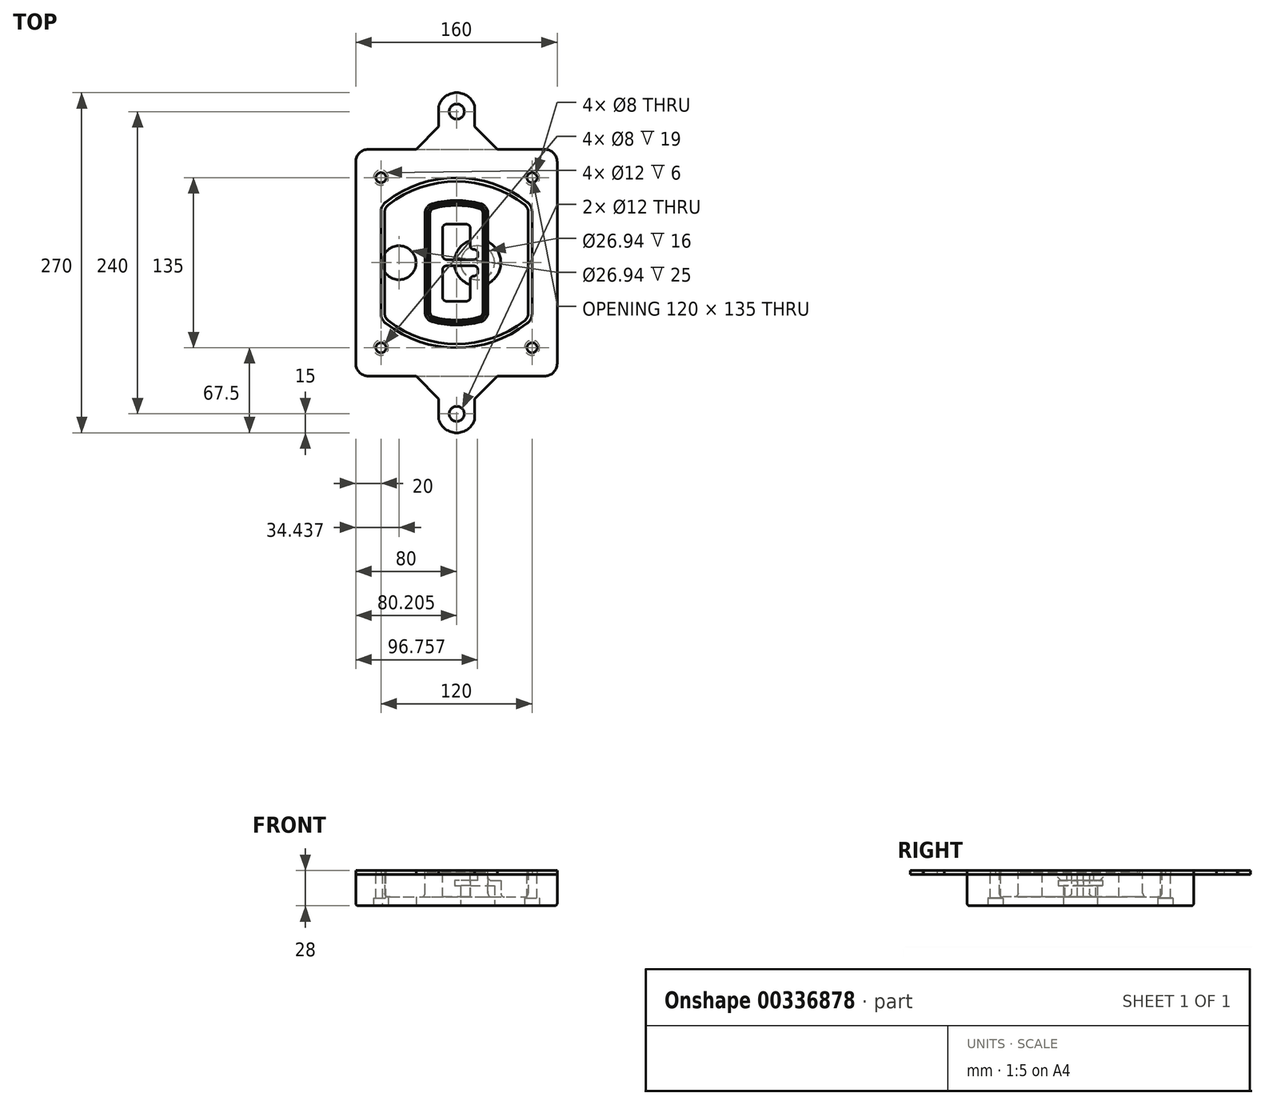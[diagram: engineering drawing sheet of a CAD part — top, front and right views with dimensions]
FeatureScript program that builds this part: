
annotation { "Feature Type Name" : "Feature", "Feature Type Description" : "" }
export const myFeature = defineFeature(function(context is Context, id is Id, definition is map)
    precondition{}
    {
        {
            var Q0;
            Q0=qCreatedBy(makeId("Top.planeOp"),FACE);
            var sketch = newSketch(context, id + "F0", { "sketchPlane" : qUnion([Q0])});
            skPoint(sketch, "E0.rect.middle", {"position": v(0, 0) * mm});
            skLineSegment(sketch, "E1.bottom", {"start": v(-70, -90) * mm, "end": v(70, -90) * mm});
            skLineSegment(sketch, "E1.top", {"start": v(-70, 90) * mm, "end": v(70, 90) * mm});
            skLineSegment(sketch, "E1.left", {"start": v(-80, -80) * mm, "end": v(-80, 80) * mm});
            skLineSegment(sketch, "E1.right", {"start": v(80, -80) * mm, "end": v(80, 80) * mm});
            skLineSegment(sketch, "E2", {"start": v(-80, 90) * mm, "end": v(80, -90) * mm, "construction": true});
            skLineSegment(sketch, "E3", {"start": v(80, 90) * mm, "end": v(-80, -90) * mm, "construction": true});
            skCircle(sketch, "E4", {"center": v(-60, 67.5) * mm, "radius": 4 * mm});
            skCircle(sketch, "E5", {"center": v(60, 67.5) * mm, "radius": 4 * mm});
            skCircle(sketch, "E6", {"center": v(60, -67.5) * mm, "radius": 4 * mm});
            skCircle(sketch, "E7", {"center": v(-60, -67.5) * mm, "radius": 4 * mm});
            skLineSegment(sketch, "E8", {"start": v(-60, 67.5) * mm, "end": v(60, 67.5) * mm, "construction": true});
            skLineSegment(sketch, "E9", {"start": v(60, 67.5) * mm, "end": v(60, -67.5) * mm, "construction": true});
            skLineSegment(sketch, "E10", {"start": v(60, -67.5) * mm, "end": v(-60, -67.5) * mm, "construction": true});
            skLineSegment(sketch, "E11", {"start": v(-60, -67.5) * mm, "end": v(-60, 67.5) * mm, "construction": true});
            skLineSegment(sketch, "E12", {"start": v(-60, 40.3) * mm, "end": v(-60, -40.3) * mm});
            skLineSegment(sketch, "E13", {"start": v(60, 40.3) * mm, "end": v(60, -40.3) * mm});
            skArc(sketch, "E14", {"start": v(56.15, 48.18) * mm, "mid": v(0, 67.5) * mm, "end": v(-56.15, 48.18) * mm});
            skArc(sketch, "E15", {"start": v(-56.15, -48.18) * mm, "mid": v(0, -67.5) * mm, "end": v(56.15, -48.18) * mm});
            skLineSegment(sketch, "E16", {"start": v(-60, 0) * mm, "end": v(60, 0) * mm, "construction": true});
            skPoint(sketch, "E17.visualSharp", {"position": v(-60, -45) * mm});
            skArc(sketch, "E17.filletArc", {"start": v(-60, -40.3) * mm, "mid": v(-58.99, -44.68) * mm, "end": v(-56.15, -48.18) * mm});
            skPoint(sketch, "E18.visualSharp", {"position": v(-60, 45) * mm});
            skArc(sketch, "E18.filletArc", {"start": v(-56.15, 48.18) * mm, "mid": v(-58.99, 44.68) * mm, "end": v(-60, 40.3) * mm});
            skPoint(sketch, "E19.visualSharp", {"position": v(60, 45) * mm});
            skArc(sketch, "E19.filletArc", {"start": v(60, 40.3) * mm, "mid": v(58.99, 44.68) * mm, "end": v(56.15, 48.18) * mm});
            skPoint(sketch, "E20.visualSharp", {"position": v(60, -45) * mm});
            skArc(sketch, "E20.filletArc", {"start": v(56.15, -48.18) * mm, "mid": v(58.99, -44.68) * mm, "end": v(60, -40.3) * mm});
            skPoint(sketch, "E21.visualSharp", {"position": v(-80, 90) * mm});
            skArc(sketch, "E21.filletArc", {"start": v(-70, 90) * mm, "mid": v(-77.07, 87.07) * mm, "end": v(-80, 80) * mm});
            skPoint(sketch, "E22.visualSharp", {"position": v(80, 90) * mm});
            skArc(sketch, "E22.filletArc", {"start": v(80, 80) * mm, "mid": v(77.07, 87.07) * mm, "end": v(70, 90) * mm});
            skPoint(sketch, "E23.visualSharp", {"position": v(80, -90) * mm});
            skArc(sketch, "E23.filletArc", {"start": v(70, -90) * mm, "mid": v(77.07, -87.07) * mm, "end": v(80, -80) * mm});
            skPoint(sketch, "E24.visualSharp", {"position": v(-80, -90) * mm});
            skArc(sketch, "E24.filletArc", {"start": v(-80, -80) * mm, "mid": v(-77.07, -87.07) * mm, "end": v(-70, -90) * mm});
            skArc(sketch, "E25.0", {"start": v(57, 40.3) * mm, "mid": v(56.3, 43.36) * mm, "end": v(54.3, 45.81) * mm});
            skLineSegment(sketch, "E25.1", {"start": v(57, 40.3) * mm, "end": v(57, -40.3) * mm});
            skArc(sketch, "E25.2", {"start": v(54.3, -45.81) * mm, "mid": v(56.3, -43.36) * mm, "end": v(57, -40.3) * mm});
            skArc(sketch, "E25.3", {"start": v(-54.3, -45.81) * mm, "mid": v(0, -64.5) * mm, "end": v(54.3, -45.81) * mm});
            skArc(sketch, "E25.4", {"start": v(-57, -40.3) * mm, "mid": v(-56.3, -43.36) * mm, "end": v(-54.3, -45.81) * mm});
            skArc(sketch, "E25.5", {"start": v(54.3, 45.81) * mm, "mid": v(0, 64.5) * mm, "end": v(-54.3, 45.81) * mm});
            skLineSegment(sketch, "E25.6", {"start": v(-57, 40.3) * mm, "end": v(-57, -40.3) * mm});
            skArc(sketch, "E25.7", {"start": v(-54.3, 45.81) * mm, "mid": v(-56.3, 43.36) * mm, "end": v(-57, 40.3) * mm});
            skArc(sketch, "E26.0", {"start": v(-58.62, 51.33) * mm, "mid": v(-62.58, 46.43) * mm, "end": v(-64, 40.3) * mm});
            skArc(sketch, "E26.1", {"start": v(58.62, 51.33) * mm, "mid": v(0, 71.5) * mm, "end": v(-58.62, 51.33) * mm});
            skArc(sketch, "E26.2", {"start": v(64, 40.3) * mm, "mid": v(62.58, 46.43) * mm, "end": v(58.62, 51.33) * mm});
            skLineSegment(sketch, "E26.3", {"start": v(64, 40.3) * mm, "end": v(64, -40.3) * mm});
            skArc(sketch, "E26.4", {"start": v(58.62, -51.33) * mm, "mid": v(62.58, -46.43) * mm, "end": v(64, -40.3) * mm});
            skLineSegment(sketch, "E26.5", {"start": v(-64, 40.3) * mm, "end": v(-64, -40.3) * mm});
            skArc(sketch, "E26.6", {"start": v(-58.62, -51.33) * mm, "mid": v(0, -71.5) * mm, "end": v(58.62, -51.33) * mm});
            skArc(sketch, "E26.7", {"start": v(-64, -40.3) * mm, "mid": v(-62.58, -46.43) * mm, "end": v(-58.62, -51.33) * mm});
            skSolve(sketch);
        }
        {
            var Q0;
            Q0=makeQuery(id+"F0.imprint","IMPRINT",FACE,{"disambiguationData":[TD([[makeQuery(id+"F0.imprint","IMPRINT",EDGE,{"derivedFrom":sQuery(id+"F0.wireOp",EDGE,"E1.bottom")}),1.0]])]});
            var Q1;
            Q1=makeQuery(id+"F0.imprint","IMPRINT",FACE,{"disambiguationData":[TD([[makeQuery(id+"F0.imprint","IMPRINT",EDGE,{"derivedFrom":sQuery(id+"F0.wireOp",EDGE,"E12")}),1.0]])]});
            var Q2;
            Q2=makeQuery(id+"F0.imprint","IMPRINT",FACE,{"disambiguationData":[TD([[makeQuery(id+"F0.imprint","IMPRINT",EDGE,{"derivedFrom":sQuery(id+"F0.wireOp",EDGE,"E25.0")}),1.0]])]});
            var Q3;
            Q3=makeQuery(id+"F0.imprint","IMPRINT",FACE,{"disambiguationData":[TD([[makeQuery(id+"F0.imprint","IMPRINT",EDGE,{"derivedFrom":sQuery(id+"F0.wireOp",EDGE,"E12")}),-1.0]])]});
            extrude(context, id + "F1", {"entities" : qUnion([Q0, Q1, Q2, Q3]), "oppositeDirection" : true, "depth" : 25 * mm});
        }
        {
            var Q0;
            Q0=makeQuery(id+"F0.imprint","IMPRINT",FACE,{"disambiguationData":[TD([[makeQuery(id+"F0.imprint","IMPRINT",EDGE,{"derivedFrom":sQuery(id+"F0.wireOp",EDGE,"E12")}),1.0]])]});
            extrude(context, id + "F2", {"entities" : qUnion([Q0]), "operationType" : NewBodyOperationType.ADD, "depth" : 3 * mm});
        }
        {
            var Q0;
            Q0=makeQuery(id+"F0.imprint","IMPRINT",FACE,{"disambiguationData":[TD([[makeQuery(id+"F0.imprint","IMPRINT",EDGE,{"derivedFrom":sQuery(id+"F0.wireOp",EDGE,"E25.0")}),1.0]])]});
            extrude(context, id + "F3", {"entities" : qUnion([Q0]), "operationType" : NewBodyOperationType.REMOVE, "oppositeDirection" : true, "depth" : 18 * mm});
        }
        {
            var Q0;
            Q0=makeQuery(id+"F2.opExtrude","CAP_FACE",FACE,{"disambiguationData":[OSD([sQuery(id+"F0.wireOp",EDGE,"E12"),sQuery(id+"F0.wireOp",EDGE,"E13"),sQuery(id+"F0.wireOp",EDGE,"E14"),sQuery(id+"F0.wireOp",EDGE,"E15"),sQuery(id+"F0.wireOp",EDGE,"E17.filletArc"),sQuery(id+"F0.wireOp",EDGE,"E18.filletArc"),sQuery(id+"F0.wireOp",EDGE,"E19.filletArc"),sQuery(id+"F0.wireOp",EDGE,"E20.filletArc"),sQuery(id+"F0.wireOp",EDGE,"E25.0"),sQuery(id+"F0.wireOp",EDGE,"E25.1"),sQuery(id+"F0.wireOp",EDGE,"E25.2"),sQuery(id+"F0.wireOp",EDGE,"E25.3"),sQuery(id+"F0.wireOp",EDGE,"E25.4"),sQuery(id+"F0.wireOp",EDGE,"E25.5"),sQuery(id+"F0.wireOp",EDGE,"E25.6"),sQuery(id+"F0.wireOp",EDGE,"E25.7")])],"isStart":false});
            var sketch = newSketch(context, id + "F4", { "sketchPlane" : qUnion([Q0])});
            skArc(sketch, "E27.0", {"start": v(-19.08, -46.97) * mm, "mid": v(0, -49.5) * mm, "end": v(19.08, -46.97) * mm});
            skArc(sketch, "E28.0", {"start": v(19.08, 46.97) * mm, "mid": v(0, 49.5) * mm, "end": v(-19.08, 46.97) * mm});
            skLineSegment(sketch, "E29", {"start": v(-25, 39.25) * mm, "end": v(-25, -39.25) * mm});
            skLineSegment(sketch, "E30", {"start": v(25, 39.25) * mm, "end": v(25, -39.25) * mm});
            skLineSegment(sketch, "E31", {"start": v(-25, 45.1) * mm, "end": v(25, 45.1) * mm, "construction": true});
            skLineSegment(sketch, "E32", {"start": v(-25, -45.1) * mm, "end": v(25, -45.1) * mm, "construction": true});
            skPoint(sketch, "E33.visualSharp", {"position": v(-25, 45.1) * mm});
            skArc(sketch, "E33.filletArc", {"start": v(-19.08, 46.97) * mm, "mid": v(-23.35, 44.11) * mm, "end": v(-25, 39.25) * mm});
            skPoint(sketch, "E34.visualSharp", {"position": v(25, 45.1) * mm});
            skArc(sketch, "E34.filletArc", {"start": v(25, 39.25) * mm, "mid": v(23.35, 44.11) * mm, "end": v(19.08, 46.97) * mm});
            skPoint(sketch, "E35.visualSharp", {"position": v(25, -45.1) * mm});
            skArc(sketch, "E35.filletArc", {"start": v(19.08, -46.97) * mm, "mid": v(23.35, -44.11) * mm, "end": v(25, -39.25) * mm});
            skPoint(sketch, "E36.visualSharp", {"position": v(-25, -45.1) * mm});
            skArc(sketch, "E36.filletArc", {"start": v(-25, -39.25) * mm, "mid": v(-23.35, -44.11) * mm, "end": v(-19.08, -46.97) * mm});
            skArc(sketch, "E37.0", {"start": v(54.3, 45.81) * mm, "mid": v(0, 64.5) * mm, "end": v(-54.3, 45.81) * mm});
            skArc(sketch, "E37.1", {"start": v(-54.3, 45.81) * mm, "mid": v(-56.3, 43.36) * mm, "end": v(-57, 40.3) * mm});
            skLineSegment(sketch, "E37.2", {"start": v(-57, 40.3) * mm, "end": v(-57, -40.3) * mm});
            skArc(sketch, "E37.3", {"start": v(-57, -40.3) * mm, "mid": v(-56.3, -43.36) * mm, "end": v(-54.3, -45.81) * mm});
            skArc(sketch, "E37.4", {"start": v(-54.3, -45.81) * mm, "mid": v(0, -64.5) * mm, "end": v(54.3, -45.81) * mm});
            skArc(sketch, "E37.5", {"start": v(54.3, -45.81) * mm, "mid": v(56.3, -43.36) * mm, "end": v(57, -40.3) * mm});
            skLineSegment(sketch, "E37.6", {"start": v(57, 40.3) * mm, "end": v(57, -40.3) * mm});
            skArc(sketch, "E37.7", {"start": v(57, 40.3) * mm, "mid": v(56.3, 43.36) * mm, "end": v(54.3, 45.81) * mm});
            skLineSegment(sketch, "E38.0", {"start": v(23, 39.25) * mm, "end": v(23, -39.25) * mm});
            skArc(sketch, "E38.1", {"start": v(18.56, -45.04) * mm, "mid": v(21.76, -42.9) * mm, "end": v(23, -39.25) * mm});
            skArc(sketch, "E38.2", {"start": v(-18.56, -45.04) * mm, "mid": v(0, -47.5) * mm, "end": v(18.56, -45.04) * mm});
            skArc(sketch, "E38.3", {"start": v(-23, -39.25) * mm, "mid": v(-21.76, -42.9) * mm, "end": v(-18.56, -45.04) * mm});
            skLineSegment(sketch, "E38.4", {"start": v(-23, 39.25) * mm, "end": v(-23, -39.25) * mm});
            skArc(sketch, "E38.5", {"start": v(23, 39.25) * mm, "mid": v(21.76, 42.9) * mm, "end": v(18.56, 45.04) * mm});
            skArc(sketch, "E38.6", {"start": v(-18.56, 45.04) * mm, "mid": v(-21.76, 42.9) * mm, "end": v(-23, 39.25) * mm});
            skArc(sketch, "E38.7", {"start": v(18.56, 45.04) * mm, "mid": v(0, 47.5) * mm, "end": v(-18.56, 45.04) * mm});
            skArc(sketch, "E39.0", {"start": v(21, 39.25) * mm, "mid": v(20.18, 41.68) * mm, "end": v(18.04, 43.1) * mm});
            skLineSegment(sketch, "E39.1", {"start": v(21, 39.25) * mm, "end": v(21, -39.25) * mm});
            skArc(sketch, "E39.2", {"start": v(18.04, -43.1) * mm, "mid": v(20.18, -41.68) * mm, "end": v(21, -39.25) * mm});
            skArc(sketch, "E39.3", {"start": v(-18.04, -43.1) * mm, "mid": v(0, -45.5) * mm, "end": v(18.04, -43.1) * mm});
            skArc(sketch, "E39.4", {"start": v(-21, -39.25) * mm, "mid": v(-20.18, -41.68) * mm, "end": v(-18.04, -43.1) * mm});
            skArc(sketch, "E39.5", {"start": v(18.04, 43.1) * mm, "mid": v(0, 45.5) * mm, "end": v(-18.04, 43.1) * mm});
            skLineSegment(sketch, "E39.6", {"start": v(-21, 39.25) * mm, "end": v(-21, -39.25) * mm});
            skArc(sketch, "E39.7", {"start": v(-18.04, 43.1) * mm, "mid": v(-20.18, 41.68) * mm, "end": v(-21, 39.25) * mm});
            skLineSegment(sketch, "E40", {"start": v(-25, 0) * mm, "end": v(25, 0) * mm, "construction": true});
            skLineSegment(sketch, "E41", {"start": v(-11, 5.5) * mm, "end": v(-11, 27.5) * mm});
            skLineSegment(sketch, "E42", {"start": v(-8, 30.5) * mm, "end": v(8, 30.5) * mm});
            skLineSegment(sketch, "E43", {"start": v(11, 27.5) * mm, "end": v(11, 13.5) * mm});
            skLineSegment(sketch, "E44", {"start": v(14, 10.5) * mm, "end": v(14, 10.5) * mm});
            skLineSegment(sketch, "E45", {"start": v(17, 7.5) * mm, "end": v(17, 5.5) * mm});
            skLineSegment(sketch, "E46", {"start": v(14, 2.5) * mm, "end": v(-8, 2.5) * mm});
            skPoint(sketch, "E47.visualSharp", {"position": v(-11, 30.5) * mm});
            skArc(sketch, "E47.filletArc", {"start": v(-8, 30.5) * mm, "mid": v(-10.12, 29.62) * mm, "end": v(-11, 27.5) * mm});
            skPoint(sketch, "E48.visualSharp", {"position": v(11, 30.5) * mm});
            skArc(sketch, "E48.filletArc", {"start": v(11, 27.5) * mm, "mid": v(10.12, 29.62) * mm, "end": v(8, 30.5) * mm});
            skPoint(sketch, "E49.visualSharp", {"position": v(11, 10.5) * mm});
            skArc(sketch, "E49.filletArc", {"start": v(11, 13.5) * mm, "mid": v(11.88, 11.38) * mm, "end": v(14, 10.5) * mm});
            skPoint(sketch, "E50.visualSharp", {"position": v(17, 10.5) * mm});
            skArc(sketch, "E50.filletArc", {"start": v(17, 7.5) * mm, "mid": v(16.12, 9.62) * mm, "end": v(14, 10.5) * mm});
            skPoint(sketch, "E51.visualSharp", {"position": v(17, 2.5) * mm});
            skArc(sketch, "E51.filletArc", {"start": v(14, 2.5) * mm, "mid": v(16.12, 3.38) * mm, "end": v(17, 5.5) * mm});
            skPoint(sketch, "E52.visualSharp", {"position": v(-11, 2.5) * mm});
            skArc(sketch, "E52.filletArc", {"start": v(-11, 5.5) * mm, "mid": v(-10.12, 3.38) * mm, "end": v(-8, 2.5) * mm});
            skLineSegment(sketch, "E53.0.MirrorCS", {"start": v(14, -2.5) * mm, "end": v(-8, -2.5) * mm});
            skArc(sketch, "E54.0.MirrorCS", {"start": v(-11, -5.5) * mm, "mid": v(-10.12, -3.38) * mm, "end": v(-8, -2.5) * mm});
            skLineSegment(sketch, "E55.0.MirrorCS", {"start": v(-11, -5.5) * mm, "end": v(-11, -27.5) * mm});
            skArc(sketch, "E56.0.MirrorCS", {"start": v(-8, -30.5) * mm, "mid": v(-10.12, -29.62) * mm, "end": v(-11, -27.5) * mm});
            skLineSegment(sketch, "E57.0.MirrorCS", {"start": v(-8, -30.5) * mm, "end": v(8, -30.5) * mm});
            skArc(sketch, "E58.0.MirrorCS", {"start": v(11, -27.5) * mm, "mid": v(10.12, -29.62) * mm, "end": v(8, -30.5) * mm});
            skLineSegment(sketch, "E59.0.MirrorCS", {"start": v(11, -27.5) * mm, "end": v(11, -13.5) * mm});
            skArc(sketch, "E60.0.MirrorCS", {"start": v(11, -13.5) * mm, "mid": v(11.88, -11.38) * mm, "end": v(14, -10.5) * mm});
            skArc(sketch, "E61.0.MirrorCS", {"start": v(17, -7.5) * mm, "mid": v(16.12, -9.62) * mm, "end": v(14, -10.5) * mm});
            skLineSegment(sketch, "E62.0.MirrorCS", {"start": v(17, -7.5) * mm, "end": v(17, -5.5) * mm});
            skArc(sketch, "E63.0.MirrorCS", {"start": v(14, -2.5) * mm, "mid": v(16.12, -3.38) * mm, "end": v(17, -5.5) * mm});
            skSolve(sketch);
        }
        {
            var Q0;
            Q0=makeQuery(id+"F4.imprint","IMPRINT",FACE,{"disambiguationData":[TD([[makeQuery(id+"F4.imprint","IMPRINT",EDGE,{"derivedFrom":sQuery(id+"F4.wireOp",EDGE,"E27.0")}),1.0]])]});
            var Q1;
            Q1=makeQuery(id+"F4.imprint","IMPRINT",FACE,{"disambiguationData":[TD([[makeQuery(id+"F4.imprint","IMPRINT",EDGE,{"derivedFrom":sQuery(id+"F4.wireOp",EDGE,"E38.0")}),-1.0]])]});
            var Q2;
            Q2=makeQuery(id+"F4.imprint","IMPRINT",FACE,{"disambiguationData":[TD([[makeQuery(id+"F4.imprint","IMPRINT",EDGE,{"derivedFrom":sQuery(id+"F4.wireOp",EDGE,"E39.0")}),1.0]])]});
            extrude(context, id + "F5", {"entities" : qUnion([Q0, Q1, Q2]), "operationType" : NewBodyOperationType.ADD, "endBound" : BoundingType.UP_TO_NEXT, "oppositeDirection" : true, "depth" : 25 * mm});
        }
        {
            var Q0;
            Q0=makeQuery(id+"F4.imprint","IMPRINT",FACE,{"disambiguationData":[TD([[makeQuery(id+"F4.imprint","IMPRINT",EDGE,{"derivedFrom":sQuery(id+"F4.wireOp",EDGE,"E38.0")}),-1.0]])]});
            extrude(context, id + "F6", {"entities" : qUnion([Q0]), "operationType" : NewBodyOperationType.REMOVE, "oppositeDirection" : true, "depth" : 2 * mm});
        }
        {
            var Q0;
            Q0=makeQuery(id+"F1.opExtrude","CAP_FACE",FACE,{"disambiguationData":[OSD([sQuery(id+"F0.wireOp",EDGE,"E1.bottom"),sQuery(id+"F0.wireOp",EDGE,"E1.top"),sQuery(id+"F0.wireOp",EDGE,"E1.left"),sQuery(id+"F0.wireOp",EDGE,"E1.right"),sQuery(id+"F0.wireOp",EDGE,"E4"),sQuery(id+"F0.wireOp",EDGE,"E5"),sQuery(id+"F0.wireOp",EDGE,"E6"),sQuery(id+"F0.wireOp",EDGE,"E7"),sQuery(id+"F0.wireOp",EDGE,"E21.filletArc"),sQuery(id+"F0.wireOp",EDGE,"E22.filletArc"),sQuery(id+"F0.wireOp",EDGE,"E23.filletArc"),sQuery(id+"F0.wireOp",EDGE,"E24.filletArc")])],"isStart":false});
            var sketch = newSketch(context, id + "F7", { "sketchPlane" : qUnion([Q0])});
            skCircle(sketch, "E64", {"center": v(16.76, 0) * mm, "radius": 13.47 * mm});
            skCircle(sketch, "E65", {"center": v(-45.56, 0) * mm, "radius": 13.47 * mm});
            skLineSegment(sketch, "E66", {"start": v(80, 0) * mm, "end": v(-80, 0) * mm});
            skCircle(sketch, "E67", {"center": v(16.76, 0) * mm, "radius": 18.47 * mm});
            skCircle(sketch, "E68", {"center": v(60, -67.5) * mm, "radius": 6 * mm});
            skCircle(sketch, "E69", {"center": v(-60, -67.5) * mm, "radius": 6 * mm});
            skCircle(sketch, "E70", {"center": v(-60, 67.5) * mm, "radius": 6 * mm});
            skCircle(sketch, "E71", {"center": v(60, 67.5) * mm, "radius": 6 * mm});
            skSolve(sketch);
        }
        {
            var Q0;
            {var subQ1=sQuery(id+"F7.wireOp",EDGE,"E66");var subQ4=sQuery(id+"F7.wireOp",EDGE,"E64");var subQ6=makeQuery(id+"F7.imprint","INTERSECT",VERTEX,{"disambiguationData":[OD(0.0)],"derivedFrom":[subQ4,subQ1]});Q0=makeQuery(id+"F7.imprint","IMPRINT",FACE,{"disambiguationData":[TD([[makeQuery(id+"F7.imprint","IMPRINT",EDGE,{"disambiguationData":[TD([[subQ6,-1.0]])],"derivedFrom":subQ4}),-1.0]])]});}
            var Q1;
            {var subQ0=sQuery(id+"F7.wireOp",EDGE,"E66");var subQ1=sQuery(id+"F7.wireOp",EDGE,"E64");var subQ3=makeQuery(id+"F7.imprint","INTERSECT",VERTEX,{"disambiguationData":[OD(0.0)],"derivedFrom":[subQ1,subQ0]});Q1=makeQuery(id+"F7.imprint","IMPRINT",FACE,{"disambiguationData":[TD([[makeQuery(id+"F7.imprint","IMPRINT",EDGE,{"disambiguationData":[TD([[subQ3,-1.0]])],"derivedFrom":subQ1}),1.0]])]});}
            var Q2;
            {var subQ0=sQuery(id+"F7.wireOp",EDGE,"E66");var subQ1=sQuery(id+"F7.wireOp",EDGE,"E64");var subQ3=makeQuery(id+"F7.imprint","INTERSECT",VERTEX,{"disambiguationData":[OD(0.0)],"derivedFrom":[subQ1,subQ0]});Q2=makeQuery(id+"F7.imprint","IMPRINT",FACE,{"disambiguationData":[TD([[makeQuery(id+"F7.imprint","IMPRINT",EDGE,{"disambiguationData":[TD([[subQ3,1.0]])],"derivedFrom":subQ1}),1.0]])]});}
            var Q3;
            {var subQ1=sQuery(id+"F7.wireOp",EDGE,"E66");var subQ4=sQuery(id+"F7.wireOp",EDGE,"E64");var subQ6=makeQuery(id+"F7.imprint","INTERSECT",VERTEX,{"disambiguationData":[OD(0.0)],"derivedFrom":[subQ4,subQ1]});Q3=makeQuery(id+"F7.imprint","IMPRINT",FACE,{"disambiguationData":[TD([[makeQuery(id+"F7.imprint","IMPRINT",EDGE,{"disambiguationData":[TD([[subQ6,1.0]])],"derivedFrom":subQ4}),-1.0]])]});}
            extrude(context, id + "F8", {"entities" : qUnion([Q0, Q1, Q2, Q3]), "operationType" : NewBodyOperationType.ADD, "oppositeDirection" : true, "depth" : 20 * mm});
        }
        {
            var Q0;
            {var subQ0=sQuery(id+"F7.wireOp",EDGE,"E66");var subQ1=sQuery(id+"F7.wireOp",EDGE,"E64");var subQ3=makeQuery(id+"F7.imprint","INTERSECT",VERTEX,{"disambiguationData":[OD(0.0)],"derivedFrom":[subQ1,subQ0]});Q0=makeQuery(id+"F7.imprint","IMPRINT",FACE,{"disambiguationData":[TD([[makeQuery(id+"F7.imprint","IMPRINT",EDGE,{"disambiguationData":[TD([[subQ3,-1.0]])],"derivedFrom":subQ1}),1.0]])]});}
            var Q1;
            {var subQ0=sQuery(id+"F7.wireOp",EDGE,"E66");var subQ1=sQuery(id+"F7.wireOp",EDGE,"E64");var subQ3=makeQuery(id+"F7.imprint","INTERSECT",VERTEX,{"disambiguationData":[OD(0.0)],"derivedFrom":[subQ1,subQ0]});Q1=makeQuery(id+"F7.imprint","IMPRINT",FACE,{"disambiguationData":[TD([[makeQuery(id+"F7.imprint","IMPRINT",EDGE,{"disambiguationData":[TD([[subQ3,1.0]])],"derivedFrom":subQ1}),1.0]])]});}
            extrude(context, id + "F9", {"entities" : qUnion([Q0, Q1]), "operationType" : NewBodyOperationType.REMOVE, "oppositeDirection" : true, "depth" : 16 * mm});
        }
        {
            var Q0;
            {var subQ0=sQuery(id+"F7.wireOp",EDGE,"E66");var subQ1=sQuery(id+"F7.wireOp",EDGE,"E65");var subQ3=makeQuery(id+"F7.imprint","INTERSECT",VERTEX,{"disambiguationData":[OD(0.0)],"derivedFrom":[subQ1,subQ0]});Q0=makeQuery(id+"F7.imprint","IMPRINT",FACE,{"disambiguationData":[TD([[makeQuery(id+"F7.imprint","IMPRINT",EDGE,{"disambiguationData":[TD([[subQ3,-1.0]])],"derivedFrom":subQ1}),1.0]])]});}
            var Q1;
            {var subQ0=sQuery(id+"F7.wireOp",EDGE,"E66");var subQ1=sQuery(id+"F7.wireOp",EDGE,"E65");var subQ3=makeQuery(id+"F7.imprint","INTERSECT",VERTEX,{"disambiguationData":[OD(0.0)],"derivedFrom":[subQ1,subQ0]});Q1=makeQuery(id+"F7.imprint","IMPRINT",FACE,{"disambiguationData":[TD([[makeQuery(id+"F7.imprint","IMPRINT",EDGE,{"disambiguationData":[TD([[subQ3,1.0]])],"derivedFrom":subQ1}),1.0]])]});}
            extrude(context, id + "F10", {"entities" : qUnion([Q0, Q1]), "operationType" : NewBodyOperationType.REMOVE, "oppositeDirection" : true, "depth" : 25 * mm});
        }
        {
            var Q0;
            Q0=makeQuery(id+"F7.imprint","IMPRINT",FACE,{"disambiguationData":[TD([[makeQuery(id+"F7.imprint","IMPRINT",EDGE,{"derivedFrom":sQuery(id+"F7.wireOp",EDGE,"E68")}),1.0]])]});
            var Q1;
            Q1=makeQuery(id+"F7.imprint","IMPRINT",FACE,{"disambiguationData":[TD([[makeQuery(id+"F7.imprint","IMPRINT",EDGE,{"derivedFrom":makeQuery(id+"F1.opExtrude","CAP_EDGE",EDGE,{"disambiguationData":[OSD([sQuery(id+"F0.wireOp",EDGE,"E5")])],"isStart":false})}),-1.0]])]});
            var Q2;
            Q2=makeQuery(id+"F7.imprint","IMPRINT",FACE,{"disambiguationData":[TD([[makeQuery(id+"F7.imprint","IMPRINT",EDGE,{"derivedFrom":sQuery(id+"F7.wireOp",EDGE,"E69")}),1.0]])]});
            var Q3;
            Q3=makeQuery(id+"F7.imprint","IMPRINT",FACE,{"disambiguationData":[TD([[makeQuery(id+"F7.imprint","IMPRINT",EDGE,{"derivedFrom":makeQuery(id+"F1.opExtrude","CAP_EDGE",EDGE,{"disambiguationData":[OSD([sQuery(id+"F0.wireOp",EDGE,"E4")])],"isStart":false})}),-1.0]])]});
            var Q4;
            Q4=makeQuery(id+"F7.imprint","IMPRINT",FACE,{"disambiguationData":[TD([[makeQuery(id+"F7.imprint","IMPRINT",EDGE,{"derivedFrom":sQuery(id+"F7.wireOp",EDGE,"E70")}),1.0]])]});
            var Q5;
            Q5=makeQuery(id+"F7.imprint","IMPRINT",FACE,{"disambiguationData":[TD([[makeQuery(id+"F7.imprint","IMPRINT",EDGE,{"derivedFrom":makeQuery(id+"F1.opExtrude","CAP_EDGE",EDGE,{"disambiguationData":[OSD([sQuery(id+"F0.wireOp",EDGE,"E7")])],"isStart":false})}),-1.0]])]});
            var Q6;
            Q6=makeQuery(id+"F7.imprint","IMPRINT",FACE,{"disambiguationData":[TD([[makeQuery(id+"F7.imprint","IMPRINT",EDGE,{"derivedFrom":sQuery(id+"F7.wireOp",EDGE,"E71")}),1.0]])]});
            var Q7;
            Q7=makeQuery(id+"F7.imprint","IMPRINT",FACE,{"disambiguationData":[TD([[makeQuery(id+"F7.imprint","IMPRINT",EDGE,{"derivedFrom":makeQuery(id+"F1.opExtrude","CAP_EDGE",EDGE,{"disambiguationData":[OSD([sQuery(id+"F0.wireOp",EDGE,"E6")])],"isStart":false})}),-1.0]])]});
            extrude(context, id + "F11", {"entities" : qUnion([Q0, Q1, Q2, Q3, Q4, Q5, Q6, Q7]), "operationType" : NewBodyOperationType.REMOVE, "oppositeDirection" : true, "depth" : 6 * mm});
        }
        {
            var Q0;
            Q0=makeQuery(id+"F9.boolean.opBoolean","COPY",FACE,{"derivedFrom":makeQuery(id+"F9.opExtrude","CAP_FACE",FACE,{"disambiguationData":[OSD([sQuery(id+"F7.wireOp",EDGE,"E64")])],"isStart":false})});
            var sketch = newSketch(context, id + "F12", { "sketchPlane" : qUnion([Q0])});
            skArc(sketch, "E72.0", {"start": v(11, 17.55) * mm, "mid": v(2.57, 11.82) * mm, "end": v(-1.54, 2.5) * mm});
            skArc(sketch, "E72.1", {"start": v(-1.54, -2.5) * mm, "mid": v(2.57, -11.82) * mm, "end": v(11, -17.55) * mm});
            skLineSegment(sketch, "E73", {"start": v(-1.54, -2.5) * mm, "end": v(14, -2.5) * mm});
            skLineSegment(sketch, "E74.0", {"start": v(14, 2.5) * mm, "end": v(-1.54, 2.5) * mm});
            skArc(sketch, "E74.1", {"start": v(14, 2.5) * mm, "mid": v(16.12, 3.38) * mm, "end": v(17, 5.5) * mm});
            skLineSegment(sketch, "E74.2", {"start": v(17, 7.5) * mm, "end": v(17, 5.5) * mm});
            skArc(sketch, "E74.3", {"start": v(17, 7.5) * mm, "mid": v(16.12, 9.62) * mm, "end": v(14, 10.5) * mm});
            skArc(sketch, "E74.4", {"start": v(11, 13.5) * mm, "mid": v(11.88, 11.38) * mm, "end": v(14, 10.5) * mm});
            skLineSegment(sketch, "E74.5", {"start": v(11, 17.55) * mm, "end": v(11, 13.5) * mm});
            skLineSegment(sketch, "E74.7", {"start": v(14, -2.5) * mm, "end": v(-1.54, -2.5) * mm});
            skArc(sketch, "E74.8", {"start": v(14, -2.5) * mm, "mid": v(16.12, -3.38) * mm, "end": v(17, -5.5) * mm});
            skLineSegment(sketch, "E74.9", {"start": v(17, -7.5) * mm, "end": v(17, -5.5) * mm});
            skArc(sketch, "E74.10", {"start": v(17, -7.5) * mm, "mid": v(16.12, -9.62) * mm, "end": v(14, -10.5) * mm});
            skArc(sketch, "E74.11", {"start": v(11, -13.5) * mm, "mid": v(11.88, -11.38) * mm, "end": v(14, -10.5) * mm});
            skLineSegment(sketch, "E74.12", {"start": v(11, -17.55) * mm, "end": v(11, -13.5) * mm});
            skPoint(sketch, "E75.orphan", {"position": v(11, -27.5) * mm});
            skPoint(sketch, "E76.orphan", {"position": v(-8, -2.5) * mm});
            skPoint(sketch, "E77.orphan", {"position": v(-8, 2.5) * mm});
            skPoint(sketch, "E78.orphan", {"position": v(11, 27.5) * mm});
            skSolve(sketch);
        }
        {
            var Q0;
            {var subQ7=sQuery(id+"F12.wireOp",EDGE,"E72.0");var subQ14=sQuery(id+"F12.wireOp",EDGE,"E72.1");var subQ16=sQuery(id+"F12.wireOp",EDGE,"E74.1");var subQ18=sQuery(id+"F12.wireOp",EDGE,"E74.8");Q0=qUnion([makeQuery(id+"F12.imprint","IMPRINT",FACE,{"disambiguationData":[TD([[makeQuery(id+"F12.imprint","IMPRINT",EDGE,{"derivedFrom":subQ7}),1.0]])]}),makeQuery(id+"F12.imprint","IMPRINT",FACE,{"disambiguationData":[TD([[makeQuery(id+"F12.imprint","IMPRINT",EDGE,{"derivedFrom":subQ14}),1.0]])]}),makeQuery(id+"F12.imprint","IMPRINT",FACE,{"disambiguationData":[TD([[makeQuery(id+"F12.imprint","IMPRINT",EDGE,{"derivedFrom":subQ16}),1.0]])]}),makeQuery(id+"F12.imprint","IMPRINT",FACE,{"disambiguationData":[TD([[makeQuery(id+"F12.imprint","IMPRINT",EDGE,{"derivedFrom":subQ18}),-1.0]])]})]);}
            var Q1;
            Q1=makeQuery(id+"F5.boolean.opBoolean","SPLIT",FACE,{"disambiguationData":[TD([makeQuery(id+"F5.opExtrude","SWEPT_FACE",FACE,{"disambiguationData":[OSD([sQuery(id+"F4.wireOp",EDGE,"E41")])]})])],"derivedFrom":makeQuery(id+"F3.boolean.opBoolean","COPY",FACE,{"derivedFrom":makeQuery(id+"F3.opExtrude","CAP_FACE",FACE,{"disambiguationData":[OSD([sQuery(id+"F0.wireOp",EDGE,"E25.0"),sQuery(id+"F0.wireOp",EDGE,"E25.1"),sQuery(id+"F0.wireOp",EDGE,"E25.2"),sQuery(id+"F0.wireOp",EDGE,"E25.3"),sQuery(id+"F0.wireOp",EDGE,"E25.4"),sQuery(id+"F0.wireOp",EDGE,"E25.5"),sQuery(id+"F0.wireOp",EDGE,"E25.6"),sQuery(id+"F0.wireOp",EDGE,"E25.7")])],"isStart":false})})});
            extrude(context, id + "F13", {"entities" : qUnion([Q0]), "operationType" : NewBodyOperationType.REMOVE, "endBound" : BoundingType.UP_TO_SURFACE, "endBoundEntityFace" : qUnion([Q1]), "depth" : 25 * mm});
        }
        {
            var Q0;
            Q0=makeQuery(id+"F3.boolean.opBoolean","COPY",EDGE,{"derivedFrom":makeQuery(id+"F3.opExtrude","CAP_EDGE",EDGE,{"disambiguationData":[OSD([sQuery(id+"F0.wireOp",EDGE,"E25.6")])],"isStart":false})});
            var Q1;
            Q1=makeQuery(id+"F8.boolean.opBoolean","INTERSECT",EDGE,{"derivedFrom":[makeQuery(id+"F5.opExtrude","SWEPT_FACE",FACE,{"disambiguationData":[OSD([sQuery(id+"F4.wireOp",EDGE,"E30")])]}),makeQuery(id+"F8.opExtrude","CAP_FACE",FACE,{"disambiguationData":[OSD([sQuery(id+"F7.wireOp",EDGE,"E67")])],"isStart":false})]});
            var Q2;
            Q2=makeQuery(id+"F8.boolean.opBoolean","INTERSECT",EDGE,{"disambiguationData":[OD(1.0)],"derivedFrom":[makeQuery(id+"F5.opExtrude","SWEPT_FACE",FACE,{"disambiguationData":[OSD([sQuery(id+"F4.wireOp",EDGE,"E30")])]}),makeQuery(id+"F8.opExtrude","SWEPT_FACE",FACE,{"disambiguationData":[OSD([sQuery(id+"F7.wireOp",EDGE,"E67")])]})]});
            var Q3;
            {var subQ0=sQuery(id+"F4.wireOp",EDGE,"E30");Q3=makeQuery(id+"F8.boolean.opBoolean","SPLIT",EDGE,{"disambiguationData":[TD([makeQuery(id+"F5.opExtrude","SWEPT_FACE",FACE,{"disambiguationData":[OSD([sQuery(id+"F4.wireOp",EDGE,"E35.filletArc")])]})])],"derivedFrom":makeQuery(id+"F5.opExtrude","CAP_EDGE",EDGE,{"disambiguationData":[OSD([subQ0])],"isStart":false})});}
            var Q4;
            {var subQ0=sQuery(id+"F0.wireOp",EDGE,"E25.7");var subQ1=sQuery(id+"F0.wireOp",EDGE,"E25.1");var subQ2=sQuery(id+"F0.wireOp",EDGE,"E25.6");var subQ3=sQuery(id+"F0.wireOp",EDGE,"E25.5");var subQ4=sQuery(id+"F0.wireOp",EDGE,"E25.4");var subQ5=sQuery(id+"F0.wireOp",EDGE,"E25.0");var subQ6=sQuery(id+"F0.wireOp",EDGE,"E25.2");var subQ7=sQuery(id+"F0.wireOp",EDGE,"E25.3");Q4=makeQuery(id+"F8.boolean.opBoolean","INTERSECT",EDGE,{"derivedFrom":[makeQuery(id+"F5.boolean.opBoolean","SPLIT",FACE,{"disambiguationData":[TD([makeQuery(id+"F2.opExtrude","SWEPT_FACE",FACE,{"disambiguationData":[OSD([subQ5])]})])],"derivedFrom":makeQuery(id+"F3.boolean.opBoolean","COPY",FACE,{"derivedFrom":makeQuery(id+"F3.opExtrude","CAP_FACE",FACE,{"disambiguationData":[OSD([subQ5,subQ1,subQ6,subQ7,subQ4,subQ3,subQ2,subQ0])],"isStart":false})})}),makeQuery(id+"F8.opExtrude","SWEPT_FACE",FACE,{"disambiguationData":[OSD([sQuery(id+"F7.wireOp",EDGE,"E67")])]})]});}
            var Q5;
            Q5=makeQuery(id+"F8.boolean.opBoolean","INTERSECT",EDGE,{"disambiguationData":[OD(0.0)],"derivedFrom":[makeQuery(id+"F5.opExtrude","SWEPT_FACE",FACE,{"disambiguationData":[OSD([sQuery(id+"F4.wireOp",EDGE,"E30")])]}),makeQuery(id+"F8.opExtrude","SWEPT_FACE",FACE,{"disambiguationData":[OSD([sQuery(id+"F7.wireOp",EDGE,"E67")])]})]});
            fillet(context, id + "F14", {"entities" : qUnion([Q0, Q1, Q2, Q3, Q4, Q5]), "radius" : 3 * mm, "tangentPropagation" : true, "allowEdgeOverflow" : false});
        }
        {
            var Q0;
            Q0=makeQuery(id+"F1.opExtrude","CAP_EDGE",EDGE,{"disambiguationData":[OSD([sQuery(id+"F0.wireOp",EDGE,"E1.bottom")])],"isStart":false});
            fillet(context, id + "F15", {"entities" : qUnion([Q0]), "radius" : 2 * mm, "tangentPropagation" : true, "allowEdgeOverflow" : false});
        }
        {
            var Q0;
            {var subQ0=sQuery(id+"F0.wireOp",EDGE,"E21.filletArc");var subQ1=sQuery(id+"F0.wireOp",EDGE,"E7");var subQ2=sQuery(id+"F0.wireOp",EDGE,"E6");var subQ3=sQuery(id+"F0.wireOp",EDGE,"E5");var subQ4=sQuery(id+"F0.wireOp",EDGE,"E4");var subQ5=sQuery(id+"F0.wireOp",EDGE,"E22.filletArc");var subQ6=sQuery(id+"F0.wireOp",EDGE,"E1.bottom");var subQ7=sQuery(id+"F0.wireOp",EDGE,"E1.right");var subQ8=sQuery(id+"F0.wireOp",EDGE,"E1.top");var subQ9=sQuery(id+"F0.wireOp",EDGE,"E1.left");var subQ10=sQuery(id+"F0.wireOp",EDGE,"E23.filletArc");var subQ11=sQuery(id+"F0.wireOp",EDGE,"E24.filletArc");Q0=makeQuery(id+"F2.boolean.opBoolean","SPLIT",FACE,{"disambiguationData":[TD([makeQuery(id+"F1.opExtrude","SWEPT_FACE",FACE,{"disambiguationData":[OSD([subQ6])]})])],"derivedFrom":makeQuery(id+"F1.opExtrude","CAP_FACE",FACE,{"disambiguationData":[OSD([subQ6,subQ8,subQ9,subQ7,subQ4,subQ3,subQ2,subQ1,subQ0,subQ5,subQ10,subQ11])],"isStart":true})});}
            var sketch = newSketch(context, id + "F16", { "sketchPlane" : qUnion([Q0])});
            skLineSegment(sketch, "E79", {"start": v(-14.09, 108) * mm, "end": v(-14.09, 124.55) * mm});
            skLineSegment(sketch, "E80", {"start": v(14.5, 108) * mm, "end": v(14.5, 124.55) * mm});
            skArc(sketch, "E81", {"start": v(14.5, 124.55) * mm, "mid": v(0.2, 135) * mm, "end": v(-14.09, 124.55) * mm});
            skCircle(sketch, "E82", {"center": v(0.2, 120) * mm, "radius": 6 * mm});
            skLineSegment(sketch, "E83", {"start": v(0.2, 120) * mm, "end": v(0.2, 90) * mm, "construction": true});
            skLineSegment(sketch, "E84", {"start": v(14.5, 108) * mm, "end": v(32.5, 90) * mm});
            skLineSegment(sketch, "E85", {"start": v(-14.09, 108) * mm, "end": v(-32.09, 90) * mm});
            skLineSegment(sketch, "E86", {"start": v(-80, 0) * mm, "end": v(80, 0) * mm, "construction": true});
            skLineSegment(sketch, "E87.MirrorCS", {"start": v(-14.09, -108) * mm, "end": v(-32.09, -90) * mm});
            skLineSegment(sketch, "E88.MirrorCS", {"start": v(14.5, -108) * mm, "end": v(32.5, -90) * mm});
            skLineSegment(sketch, "E89.MirrorCS", {"start": v(14.5, -108) * mm, "end": v(14.5, -124.55) * mm});
            skLineSegment(sketch, "E90.MirrorCS", {"start": v(-14.09, -108) * mm, "end": v(-14.09, -124.55) * mm});
            skArc(sketch, "E91.MirrorCS", {"start": v(14.5, -124.55) * mm, "mid": v(0.2, -135) * mm, "end": v(-14.09, -124.55) * mm});
            skCircle(sketch, "E92.MirrorC", {"center": v(0.2, -120) * mm, "radius": 6 * mm});
            skLineSegment(sketch, "E93.MirrorCS", {"start": v(0.2, -120) * mm, "end": v(0.2, -90) * mm, "construction": true});
            skLineSegment(sketch, "E94", {"start": v(-32.09, 90) * mm, "end": v(32.5, 90) * mm});
            skSolve(sketch);
        }
        {
            var Q0;
            Q0=makeQuery(id+"F16.imprint","IMPRINT",FACE,{"disambiguationData":[TD([[makeQuery(id+"F16.imprint","IMPRINT",EDGE,{"derivedFrom":sQuery(id+"F16.wireOp",EDGE,"E79")}),-1.0]])]});
            var Q1;
            {var subQ5=sQuery(id+"F16.wireOp",EDGE,"E94");Q1=makeQuery(id+"F16.imprint","IMPRINT",FACE,{"disambiguationData":[TD([[makeQuery(id+"F16.imprint","IMPRINT",EDGE,{"derivedFrom":subQ5}),-1.0]])]});}
            var Q2;
            {var subQ1=sQuery(id+"F16.wireOp",EDGE,"E87.MirrorCS");Q2=makeQuery(id+"F16.imprint","IMPRINT",FACE,{"disambiguationData":[TD([[makeQuery(id+"F16.imprint","IMPRINT",EDGE,{"derivedFrom":subQ1}),-1.0]])]});}
            var Q3;
            Q3=makeQuery(id+"F2.opExtrude","CAP_FACE",FACE,{"disambiguationData":[OSD([sQuery(id+"F0.wireOp",EDGE,"E12"),sQuery(id+"F0.wireOp",EDGE,"E13"),sQuery(id+"F0.wireOp",EDGE,"E14"),sQuery(id+"F0.wireOp",EDGE,"E15"),sQuery(id+"F0.wireOp",EDGE,"E17.filletArc"),sQuery(id+"F0.wireOp",EDGE,"E18.filletArc"),sQuery(id+"F0.wireOp",EDGE,"E19.filletArc"),sQuery(id+"F0.wireOp",EDGE,"E20.filletArc"),sQuery(id+"F0.wireOp",EDGE,"E25.0"),sQuery(id+"F0.wireOp",EDGE,"E25.1"),sQuery(id+"F0.wireOp",EDGE,"E25.2"),sQuery(id+"F0.wireOp",EDGE,"E25.3"),sQuery(id+"F0.wireOp",EDGE,"E25.4"),sQuery(id+"F0.wireOp",EDGE,"E25.5"),sQuery(id+"F0.wireOp",EDGE,"E25.6"),sQuery(id+"F0.wireOp",EDGE,"E25.7")])],"isStart":false});
            extrude(context, id + "F17", {"entities" : qUnion([Q0, Q1, Q2]), "endBound" : BoundingType.UP_TO_SURFACE, "endBoundEntityFace" : qUnion([Q3]), "depth" : 25 * mm});
        }
    });
